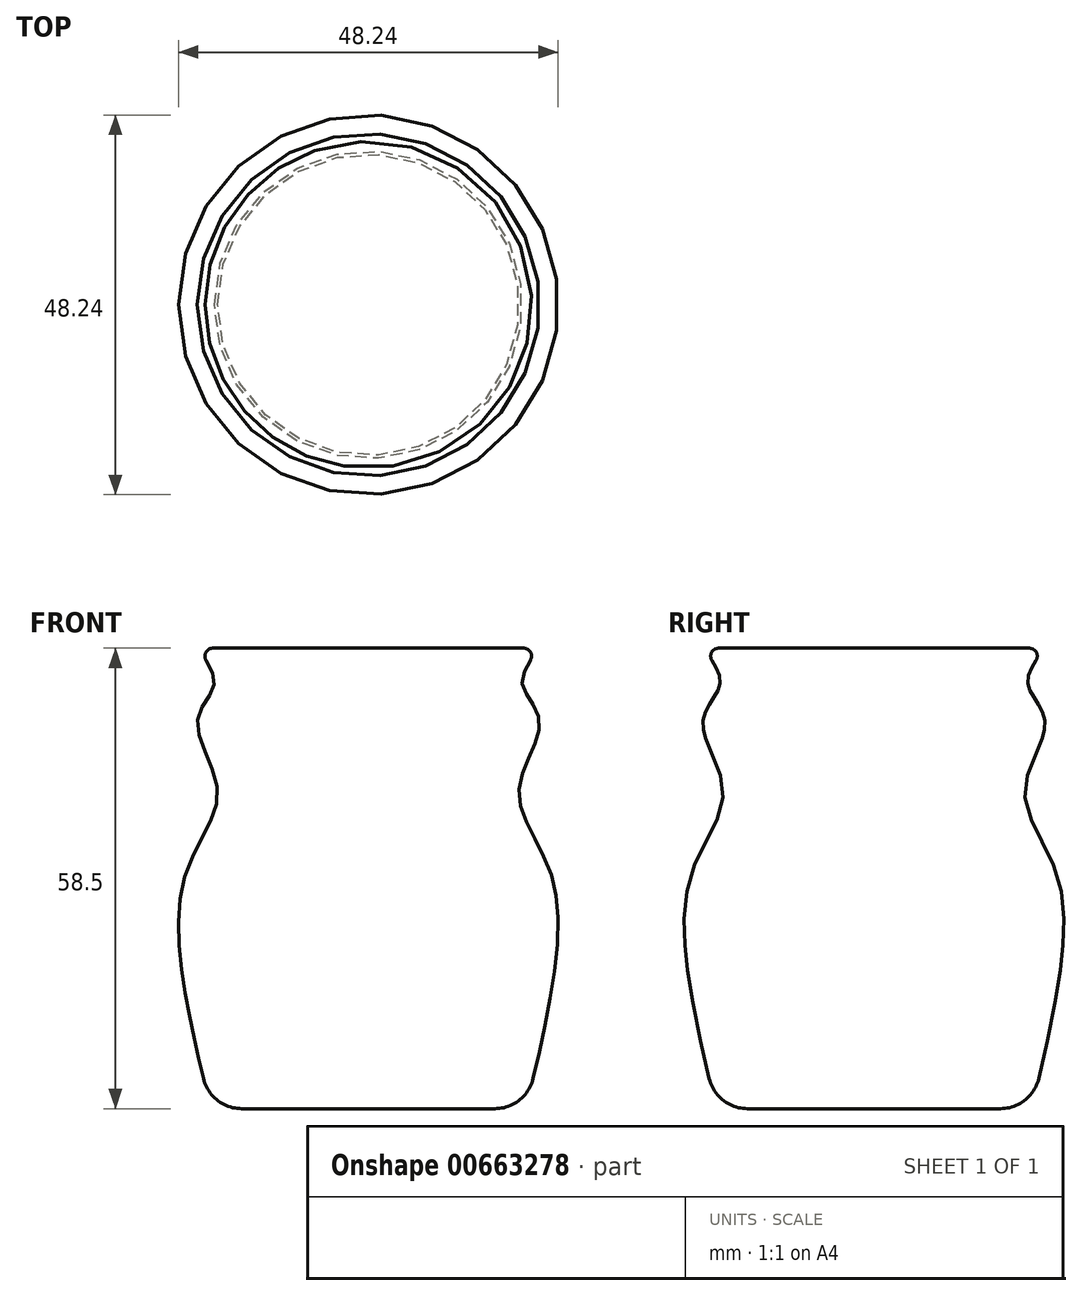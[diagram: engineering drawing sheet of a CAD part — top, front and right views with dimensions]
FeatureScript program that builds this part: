
annotation { "Feature Type Name" : "Feature", "Feature Type Description" : "" }
export const myFeature = defineFeature(function(context is Context, id is Id, definition is map)
    precondition{}
    {
        {
            var Q0;
            Q0=qCreatedBy(makeId("Front.planeOp"),FACE);
            var sketch = newSketch(context, id + "F0", { "sketchPlane" : qUnion([Q0])});
            skFitSpline(sketch, "E0", {"points": [v(-20, 0) * mm, v(-23.03, 13.51) * mm, v(-23.24, 29.73) * mm, v(-19.14, 40.32) * mm, v(-21.73, 49.19) * mm, v(-19.57, 53.95) * mm, v(-22.6, 60) * mm], "startDerivative": vector(-16.55, 66.9) * mm, "endDerivative": vector(-34.74, 56.66) * mm});
            skLineSegment(sketch, "E1", {"start": v(0, 0) * mm, "end": v(-20, 0) * mm});
            skLineSegment(sketch, "E2", {"start": v(-22.6, 60) * mm, "end": v(0, 60) * mm});
            skLineSegment(sketch, "E3", {"start": v(0, 0) * mm, "end": v(0, 60) * mm});
            skSolve(sketch);
        }
        {
            var Q0;
            Q0=makeQuery(id+"F0.imprint","IMPRINT",FACE,{"disambiguationData":[TD([[makeQuery(id+"F0.imprint","IMPRINT",EDGE,{"derivedFrom":sQuery(id+"F0.wireOp",EDGE,"E0")}),-1.0]])]});
            var Q1;
            Q1=sQuery(id+"F0.wireOp",EDGE,"E3");
            revolve(context, id + "F1", {"entities" : qUnion([Q0]), "axis" : qUnion([Q1]), "revolveType" : RevolveType.FULL});
        }
        {
            var Q0;
            Q0=makeQuery(id+"F1.opRevolve","SWEPT_FACE",FACE,{"disambiguationData":[OSD([sQuery(id+"F0.wireOp",EDGE,"E2")])]});
            var sketch = newSketch(context, id + "F2", { "sketchPlane" : qUnion([Q0])});
            skCircle(sketch, "E4", {"center": v(0, 0) * mm, "radius": 22.6 * mm});
            skSolve(sketch);
        }
        {
            var Q0;
            Q0=makeQuery(id+"F2.imprint","IMPRINT",FACE,{"disambiguationData":[TD([[makeQuery(id+"F2.imprint","IMPRINT",EDGE,{"derivedFrom":makeQuery(id+"F1.opRevolve","SWEPT_EDGE",EDGE,{"disambiguationData":[OSD([sQuery(id+"F0.wireOp",EDGE,"E0"),sQuery(id+"F0.wireOp",EDGE,"E2")])]})}),-1.0]])]});
            extrude(context, id + "F3", {"entities" : qUnion([Q0]), "operationType" : NewBodyOperationType.REMOVE, "oppositeDirection" : true, "depth" : 1.5 * mm, "offsetDistance" : 25 * mm});
        }
        {
            var Q0;
            {var subQ0=sQuery(id+"F0.wireOp",EDGE,"E0");Q0=makeQuery(id+"F3.boolean.opBoolean","INTERSECT",EDGE,{"derivedFrom":[makeQuery(id+"F1.opRevolve","SWEPT_FACE",FACE,{"disambiguationData":[OSD([subQ0])]}),makeQuery(id+"F3.opExtrude","CAP_FACE",FACE,{"disambiguationData":[OSD([subQ0,sQuery(id+"F0.wireOp",EDGE,"E2")])],"isStart":false})]});}
            fillet(context, id + "F4", {"entities" : qUnion([Q0]), "radius" : 1 * mm, "tangentPropagation" : true, "allowEdgeOverflow" : false});
        }
        {
            var Q0;
            Q0=makeQuery(id+"F1.opRevolve","SWEPT_EDGE",EDGE,{"disambiguationData":[OSD([sQuery(id+"F0.wireOp",EDGE,"E0"),sQuery(id+"F0.wireOp",EDGE,"E1")])]});
            fillet(context, id + "F5", {"entities" : qUnion([Q0]), "radius" : 5 * mm, "tangentPropagation" : true, "allowEdgeOverflow" : false});
        }
    });
